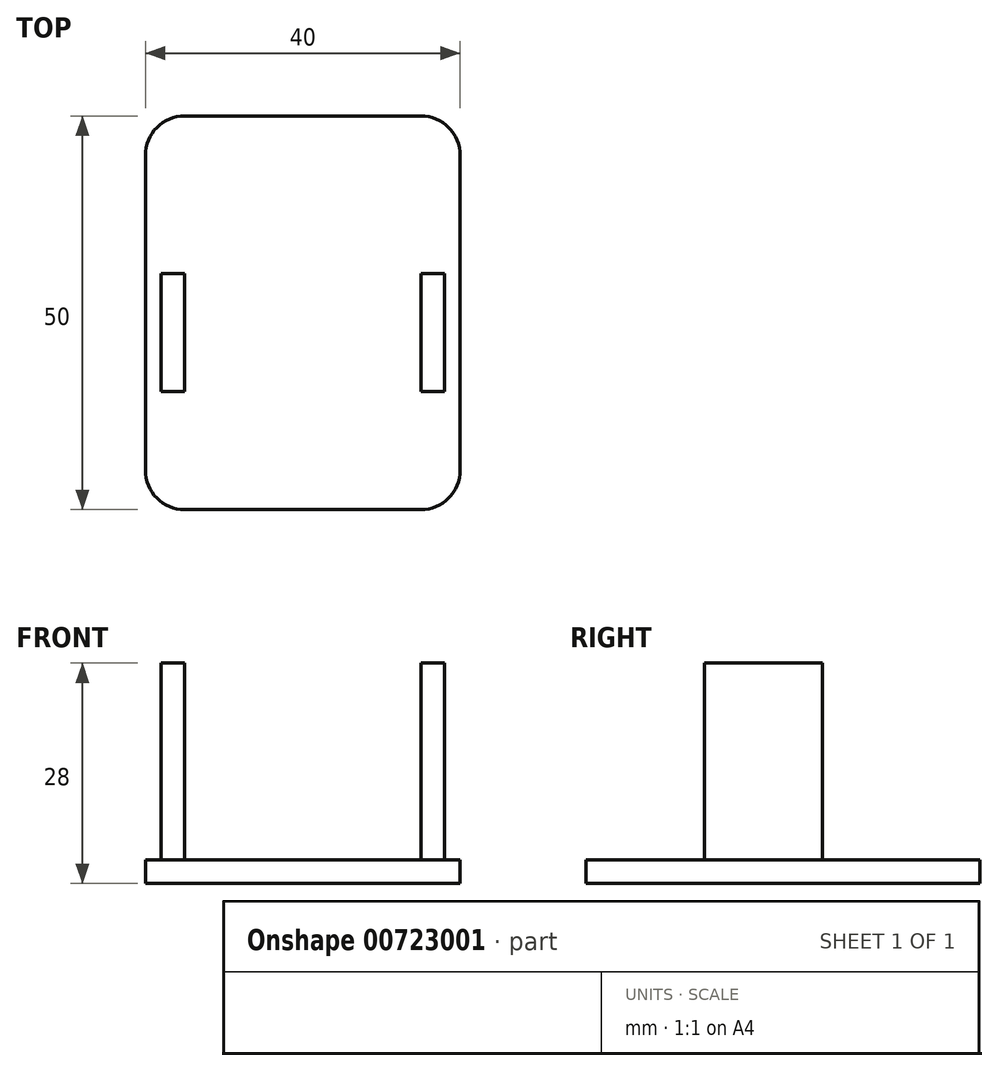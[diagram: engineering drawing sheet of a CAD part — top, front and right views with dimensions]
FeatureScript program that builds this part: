
annotation { "Feature Type Name" : "Feature", "Feature Type Description" : "" }
export const myFeature = defineFeature(function(context is Context, id is Id, definition is map)
    precondition{}
    {
        {
            var Q0;
            Q0=qCreatedBy(makeId("Top.planeOp"),FACE);
            var sketch = newSketch(context, id + "F0", { "sketchPlane" : qUnion([Q0])});
            skLineSegment(sketch, "E0.bottom", {"start": v(5, 0) * mm, "end": v(35, 0) * mm});
            skLineSegment(sketch, "E0.top", {"start": v(5, 50) * mm, "end": v(35, 50) * mm});
            skLineSegment(sketch, "E0.left", {"start": v(0, 5) * mm, "end": v(0, 45) * mm});
            skLineSegment(sketch, "E0.right", {"start": v(40, 5) * mm, "end": v(40, 45) * mm});
            skPoint(sketch, "E1.visualSharp", {"position": v(0, 50) * mm});
            skArc(sketch, "E1.filletArc", {"start": v(5, 50) * mm, "mid": v(1.46, 48.54) * mm, "end": v(0, 45) * mm});
            skPoint(sketch, "E2.visualSharp", {"position": v(40, 50) * mm});
            skArc(sketch, "E2.filletArc", {"start": v(40, 45) * mm, "mid": v(38.54, 48.54) * mm, "end": v(35, 50) * mm});
            skPoint(sketch, "E3.visualSharp", {"position": v(40, 0) * mm});
            skArc(sketch, "E3.filletArc", {"start": v(35, 0) * mm, "mid": v(38.54, 1.46) * mm, "end": v(40, 5) * mm});
            skPoint(sketch, "E4.visualSharp", {"position": v(0, 0) * mm});
            skArc(sketch, "E4.filletArc", {"start": v(0, 5) * mm, "mid": v(1.46, 1.46) * mm, "end": v(5, 0) * mm});
            skSolve(sketch);
        }
        {
            var Q0;
            Q0 = qSketchRegion(id + "F0", true);
            extrude(context, id + "F1", {"entities" : qUnion([Q0]), "depth" : 3 * mm, "offsetDistance" : 25 * mm});
        }
        {
            var Q0;
            Q0=makeQuery(id+"F1.opExtrude","CAP_FACE",FACE,{"disambiguationData":[OSD([sQuery(id+"F0.wireOp",EDGE,"E0.bottom"),sQuery(id+"F0.wireOp",EDGE,"E0.top"),sQuery(id+"F0.wireOp",EDGE,"E0.left"),sQuery(id+"F0.wireOp",EDGE,"E0.right"),sQuery(id+"F0.wireOp",EDGE,"E1.filletArc"),sQuery(id+"F0.wireOp",EDGE,"E2.filletArc"),sQuery(id+"F0.wireOp",EDGE,"E3.filletArc"),sQuery(id+"F0.wireOp",EDGE,"E4.filletArc")])],"isStart":false});
            var sketch = newSketch(context, id + "F2", { "sketchPlane" : qUnion([Q0])});
            skLineSegment(sketch, "E5", {"start": v(20, 50) * mm, "end": v(20, 0) * mm, "construction": true});
            skLineSegment(sketch, "E6.bottom", {"start": v(35, 30) * mm, "end": v(38, 30) * mm});
            skLineSegment(sketch, "E6.top", {"start": v(35, 15) * mm, "end": v(38, 15) * mm});
            skLineSegment(sketch, "E6.left", {"start": v(35, 30) * mm, "end": v(35, 15) * mm});
            skLineSegment(sketch, "E6.right", {"start": v(38, 30) * mm, "end": v(38, 15) * mm});
            skLineSegment(sketch, "E7.MirrorCS", {"start": v(5, 30) * mm, "end": v(2, 30) * mm});
            skLineSegment(sketch, "E8.MirrorCS", {"start": v(2, 30) * mm, "end": v(2, 15) * mm});
            skLineSegment(sketch, "E9.MirrorCS", {"start": v(5, 15) * mm, "end": v(2, 15) * mm});
            skLineSegment(sketch, "E10.MirrorCS", {"start": v(5, 30) * mm, "end": v(5, 15) * mm});
            skSolve(sketch);
        }
        {
            var Q0;
            Q0 = qSketchRegion(id + "F2", true);
            extrude(context, id + "F3", {"entities" : qUnion([Q0]), "operationType" : NewBodyOperationType.ADD, "depth" : 25 * mm, "offsetDistance" : 25 * mm});
        }
    });
